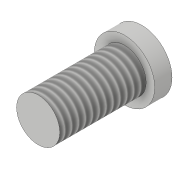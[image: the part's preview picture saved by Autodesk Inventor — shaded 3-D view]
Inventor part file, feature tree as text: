
AUTODESK INVENTOR PART (.ipt)
format: ipt  version: 2019 (Build 230136000, 136)  size: 94,720 bytes
history: native  units: in
note: dims shown in document units (in); Inventor stores cm internally (conversion verified against a paired STEP export)
features: extrude x2, sketch x2, thread x1
ambient origin geometry x8: Origin, YZ Plane, XZ Plane, XY Plane, X Axis, Y Axis, Z Axis, Center Point
bodies: Solid1 (feature_tree)
feature tree (5):
  extrude  "Extrusion1"  Depth=0.0787in TaperAngle=0.0deg
  extrude  "Extrusion2"  Depth=0.3937in TaperAngle=0.0deg
  thread  "Thread1"  [1 undecoded]
  sketch  "Sketch1"  dims[d0=0.2756in d1=0.0787in d2=0.0in]
  sketch  "Sketch2"  dims[d3=0.1969in d4=0.3937in d5=0.0in d6=0.3937in d7=0.0in]
note: 1 required parameter value undecoded (feature->parameter linkage not recoverable at this tier; creation-order binding heuristic only, values carry confidence <= 0.55)
